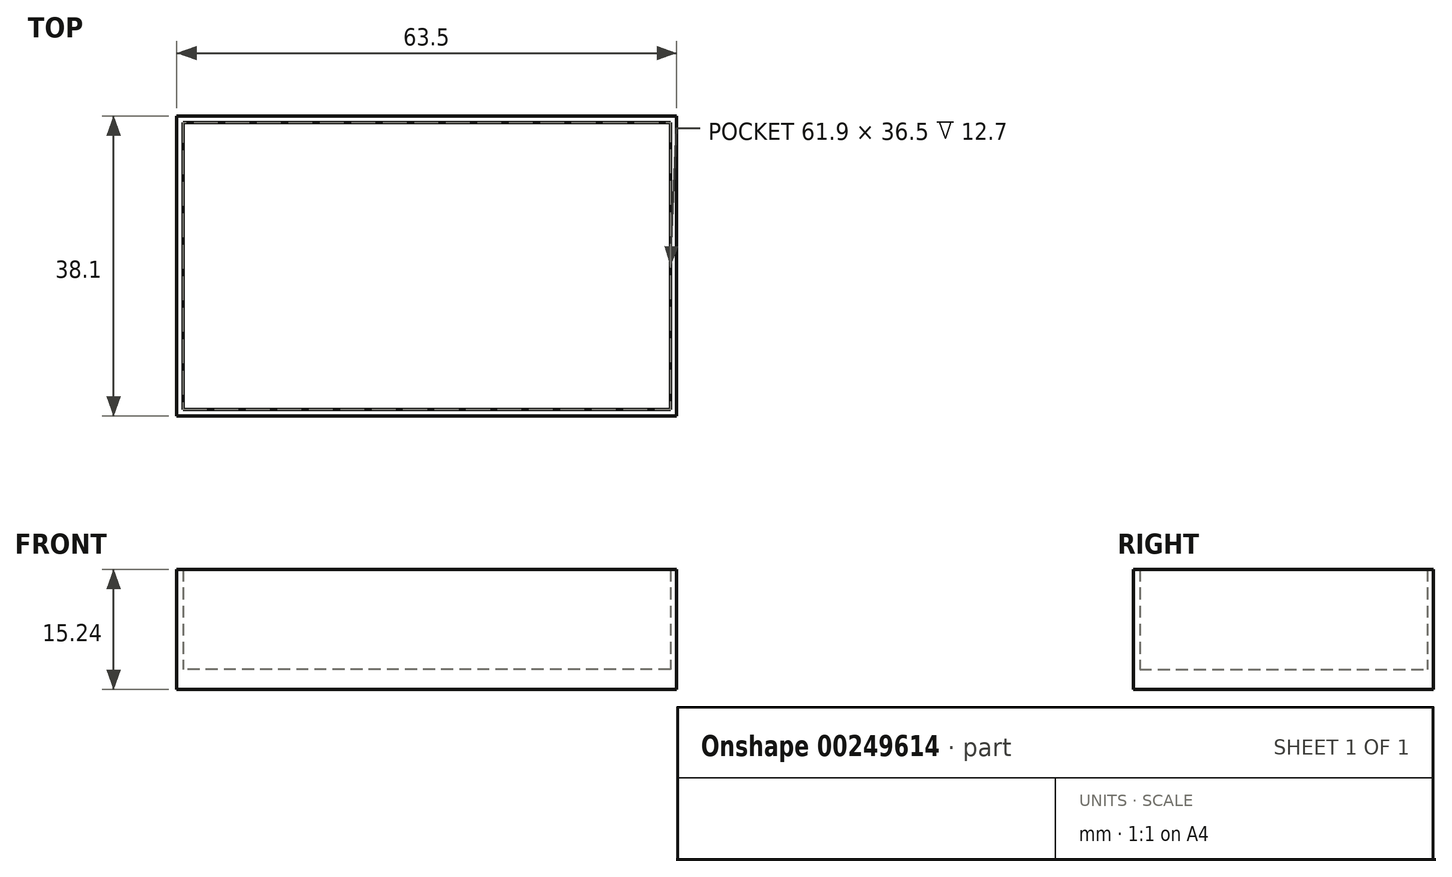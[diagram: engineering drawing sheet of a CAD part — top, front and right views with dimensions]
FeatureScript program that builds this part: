
annotation { "Feature Type Name" : "Feature", "Feature Type Description" : "" }
export const myFeature = defineFeature(function(context is Context, id is Id, definition is map)
    precondition{}
    {
        {
            var Q0;
            Q0=qCreatedBy(makeId("Top.planeOp"),FACE);
            var sketch = newSketch(context, id + "F0", { "sketchPlane" : qUnion([Q0])});
            skLineSegment(sketch, "E0.bottom", {"start": v(0, 0) * mm, "end": v(63.5, 0) * mm});
            skLineSegment(sketch, "E0.top", {"start": v(0, 38.1) * mm, "end": v(63.5, 38.1) * mm});
            skLineSegment(sketch, "E0.left", {"start": v(0, 0) * mm, "end": v(0, 38.1) * mm});
            skLineSegment(sketch, "E0.right", {"start": v(63.5, 0) * mm, "end": v(63.5, 38.1) * mm});
            skSolve(sketch);
        }
        {
            var Q0;
            Q0 = qSketchRegion(id + "F0", true);
            extrude(context, id + "F1", {"entities" : qUnion([Q0]), "depth" : 2.54 * mm});
        }
        {
            var Q0;
            Q0=makeQuery(id+"F1.opExtrude","CAP_FACE",FACE,{"disambiguationData":[OSD([sQuery(id+"F0.wireOp",EDGE,"E0.bottom"),sQuery(id+"F0.wireOp",EDGE,"E0.top"),sQuery(id+"F0.wireOp",EDGE,"E0.left"),sQuery(id+"F0.wireOp",EDGE,"E0.right")])],"isStart":false});
            var sketch = newSketch(context, id + "F2", { "sketchPlane" : qUnion([Q0])});
            skLineSegment(sketch, "E1.0", {"start": v(0, 38.1) * mm, "end": v(63.5, 38.1) * mm});
            skLineSegment(sketch, "E2.0.0", {"start": v(63.5, 38.1) * mm, "end": v(0, 38.1) * mm});
            skLineSegment(sketch, "E2.0.1", {"start": v(0, 38.1) * mm, "end": v(0, 0) * mm});
            skLineSegment(sketch, "E2.0.2", {"start": v(0, 0) * mm, "end": v(63.5, 0) * mm});
            skLineSegment(sketch, "E2.0.3", {"start": v(63.5, 0) * mm, "end": v(63.5, 38.1) * mm});
            skLineSegment(sketch, "E3.0", {"start": v(62.7, 37.3) * mm, "end": v(0.8, 37.3) * mm});
            skLineSegment(sketch, "E3.1", {"start": v(62.7, 0.8) * mm, "end": v(62.7, 37.3) * mm});
            skLineSegment(sketch, "E3.2", {"start": v(0.8, 0.8) * mm, "end": v(62.7, 0.8) * mm});
            skLineSegment(sketch, "E3.3", {"start": v(0.8, 37.3) * mm, "end": v(0.8, 0.8) * mm});
            skSolve(sketch);
        }
        {
            var Q0;
            Q0 = qSketchRegion(id + "F2", true);
            extrude(context, id + "F3", {"entities" : qUnion([Q0]), "operationType" : NewBodyOperationType.ADD, "depth" : 12.7 * mm});
        }
    });
